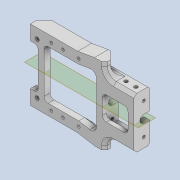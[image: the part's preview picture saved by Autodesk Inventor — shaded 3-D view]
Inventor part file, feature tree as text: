
AUTODESK INVENTOR PART (.ipt)
format: ipt  version: 2020 (Build 240168000, 168)  size: 604,160 bytes
history: native  units: mm
features: extrude x14, sketch x14, projected_geometry x14, fillet x8, thicken_offset x7, reference x5, other x5, mirror x3, chamfer x3, plane x2
ambient origin geometry x8: Origin, YZ Plane, XZ Plane, XY Plane, X Axis, Y Axis, Z Axis, Center Point
bodies: Solid1 (feature_tree)
feature tree (75):
  extrude  "Extrusion1"  Depth=7.0mm
  thicken_offset  "Thicken1"
  thicken_offset  "Thicken2"
  thicken_offset  "Thicken3"
  thicken_offset  "Thicken4"
  extrude  "Extrusion2"  Depth=7.0mm
  thicken_offset  "Thicken5"
  thicken_offset  "Thicken6"
  thicken_offset  "Thicken7"
  extrude  "Extrusion3"  Depth=21.0mm
  extrude  "Extrusion4"  Depth=4.0mm
  extrude  "Extrusion5"  Depth=4.0mm
  extrude  "Extrusion6"  Depth=15.0mm
  extrude  "Extrusion7"  Depth=15.0mm
  extrude  "Extrusion8"  Depth=4.0mm
  extrude  "Extrusion9"  Depth=3.0mm TaperAngle=0.0deg
  extrude  "Extrusion10"  Depth=1.0mm
  fillet  "Fillet1"  Radius=1.0mm
  fillet  "Fillet2"  Radius=1.0mm
  fillet  "Fillet3"  Radius=1.0mm
  fillet  "Fillet4"  Radius=1.0mm
  fillet  "Fillet5"  Radius=1.0mm
  sketch  "Sketch11"  dims[d27=1.0mm d28=7.5mm]
  plane  "Work Plane1"
  extrude  "Extrusion11"  Depth=7.5mm
  plane  "Work Plane2"
  mirror  "Mirror1"
  extrude  "Extrusion12"  Depth=15.0mm
  extrude  "Extrusion13"  Depth=4.0mm
  mirror  "Mirror2"
  extrude  "Extrusion15"  Depth=2.0mm
  mirror  "Mirror3"
  chamfer  "Chamfer1"  Distance=1.0mm
  fillet  "Fillet6"  Radius=1.0mm
  fillet  "Fillet7"  Radius=1.0mm
  chamfer  "Chamfer2"  Distance=1.0mm
  fillet  "Fillet8"  Radius=1.0mm
  chamfer  "Chamfer3"  Distance=1.5mm
  sketch  "Sketch1"  dims[d0=5.0mm d1=7.0mm]
  reference  "Reference1"
  reference  "Reference2"
  reference  "Reference3"
  sketch  "Sketch2"  dims[d2=5.0mm d3=7.0mm]
  projected_geometry  "Projected Loop1"
  sketch  "Sketch3"  dims[d4=3.0mm d5=21.0mm]
  projected_geometry  "Projected Loop2"
  sketch  "Sketch4"  dims[d6=12.0mm d7=4.0mm]
  projected_geometry  "Projected Loop3"
  sketch  "Sketch5"  dims[d8=12.0mm d9=4.0mm]
  projected_geometry  "Projected Loop4"
  sketch  "Sketch6"  dims[d10=15.0mm d11=1.745329mm]
  reference  "Reference4"
  reference  "Reference5"
  sketch  "Sketch7"  dims[d12=4.0mm d13=15.0mm]
  sketch  "Sketch8"  dims[d14=1.745329mm d15=4.0mm]
  projected_geometry  "Projected Loop5"
  projected_geometry  "Projected Loop6"
  projected_geometry  "Projected Loop7"
  projected_geometry  "Projected Loop8"
  sketch  "Sketch9"  dims[d16=3.0mm d18=3.0mm d19=0.0mm]
  projected_geometry  "Projected Loop9"
  sketch  "Sketch10"  dims[d20=1.0mm d21=1.0mm d22=1.0mm d23=1.0mm d24=1.0mm d25=1.0mm d26=1.0mm]
  projected_geometry  "Projected Loop10"
  projected_geometry  "Projected Loop11"
  sketch  "Sketch12"  dims[d29=12.0mm d30=15.0mm]
  projected_geometry  "Projected Loop12"
  sketch  "Sketch13"  dims[d31=4.0mm d32=4.0mm]
  projected_geometry  "Projected Loop13"
  sketch  "Sketch15"  dims[d33=3.0mm d34=0.0mm d35=1.0mm d36=1.0mm d37=1.0mm d38=1.0mm d39=1.0mm d40=1.0mm d41=1.5mm d42=3.0mm d43=20.0mm d44=5.0mm d45=0.0mm d46=1.5mm d47=3.0mm d48=20.0mm d49=5.0mm d50=0.0mm d51=36.0mm d52=12.0mm d53=5.0mm d54=0.0mm d55=50.0mm d56=0.0mm d57=5.0mm d58=4.0mm d59=50.0mm d60=0.0mm d61=19.0mm d62=3.0mm d63=19.0mm d64=3.0mm d65=50.0mm d66=0.0mm d67=50.0mm d68=0.0mm d69=13.0mm d70=4.0mm d71=13.0mm d72=4.0mm d73=2.0mm d74=0.0mm d75=2.0mm d76=3.0mm d77=3.0mm d78=2.0mm d79=4.5mm d80=1.5mm d81=1.5mm d82=1.5mm d83=2.0mm d84=0.0mm d85=8.0mm d86=1.8mm d87=40.0mm d88=0.0mm d89=2.5mm d90=1.4mm d91=8.0mm d92=6.0mm d93=1.4mm d94=1.4mm d95=40.0mm d96=0.0mm d103=3.0mm d104=1.8mm d105=3.0mm d106=0.0mm d107=4.0mm d108=2.0mm d109=45.0deg d110=1.0mm d111=1.0mm d112=1.5mm d113=2.0mm d114=45.0deg d115=2.0mm d116=1.0mm d117=2.0mm d118=45.0deg]
  projected_geometry  "Projected Loop15"
  parser-record x1  (decoder bookkeeping rows leaked as tree rows — omitted from the tree; the rows remain in map.json)
  other  "tip_3_n_ass.iam"
  other  "end_shell_n_1:1"
  other  "bearing_hh_1:2"
  other  "bearing_hh_1:1"
note: 1 file-system path scrubbed to <path> (originals preserved in map.json)
